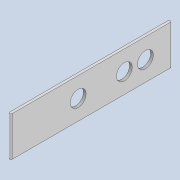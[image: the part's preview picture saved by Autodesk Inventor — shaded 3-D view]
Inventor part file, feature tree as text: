
AUTODESK INVENTOR PART (.ipt)
format: ipt  version: 2020 (Build 240168000, 168)  size: 98,816 bytes
history: native  units: mm
features: extrude x3, sketch x3
ambient origin geometry x8: Origin, YZ Plane, XZ Plane, XY Plane, X Axis, Y Axis, Z Axis, Center Point
bodies: Solid1 (feature_tree)
feature tree (6):
  extrude  "Extrusion1"  Depth=0.2mm
  extrude  "Extrusion2"  Depth=3.0mm
  extrude  "Extrusion3"  Depth=3.0mm TaperAngle=0.0deg
  sketch  "Sketch1"  dims[d0=12.0mm d1=0.2mm]
  sketch  "Sketch2"  dims[d2=3.0mm d3=0.0mm d4=2.0mm]
  sketch  "Sketch3"  dims[d5=1.2mm d6=3.0mm d7=0.0mm d8=5.0mm d9=3.5mm d10=1.2mm d11=1.2mm d12=10.0mm d13=0.0mm]
